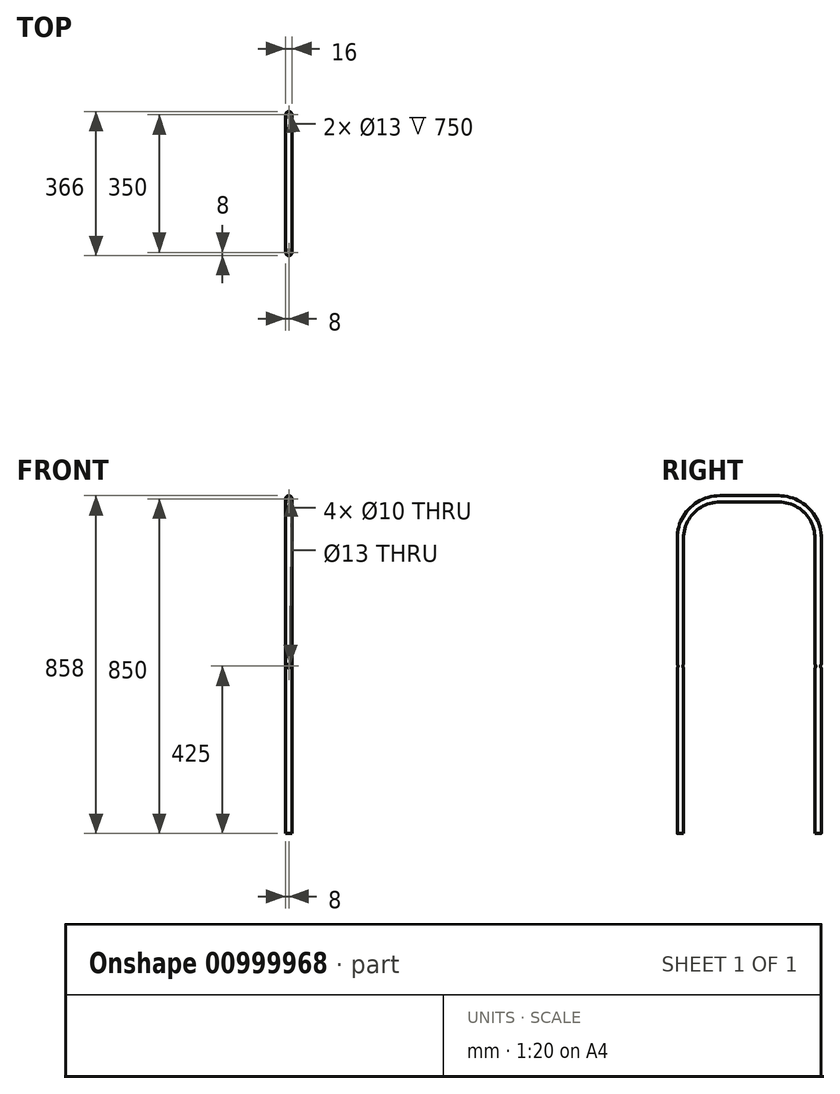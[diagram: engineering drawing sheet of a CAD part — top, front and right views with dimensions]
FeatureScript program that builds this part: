
annotation { "Feature Type Name" : "Feature", "Feature Type Description" : "" }
export const myFeature = defineFeature(function(context is Context, id is Id, definition is map)
    precondition{}
    {
        {
            var Q0;
            Q0=qCreatedBy(makeId("Right.planeOp"),FACE);
            var sketch = newSketch(context, id + "F0", { "sketchPlane" : qUnion([Q0])});
            skLineSegment(sketch, "E0.top", {"start": v(-100, 850) * mm, "end": v(-250, 850) * mm});
            skLineSegment(sketch, "E0.left", {"start": v(0, 0) * mm, "end": v(0, 750) * mm});
            skLineSegment(sketch, "E0.right", {"start": v(-350, 0) * mm, "end": v(-350, 750) * mm});
            skPoint(sketch, "E1.visualSharp", {"position": v(-350, 850) * mm});
            skArc(sketch, "E1.filletArc", {"start": v(-250, 850) * mm, "mid": v(-320.71, 820.71) * mm, "end": v(-350, 750) * mm});
            skPoint(sketch, "E2.visualSharp", {"position": v(0, 850) * mm});
            skArc(sketch, "E2.filletArc", {"start": v(0, 750) * mm, "mid": v(-29.29, 820.71) * mm, "end": v(-100, 850) * mm});
            skPoint(sketch, "E3.visualSharp", {"position": v(-16, 884) * mm});
            skPoint(sketch, "E4.visualSharp", {"position": v(-334, 884) * mm});
            skSolve(sketch);
        }
        {
            var Q0;
            Q0=qCreatedBy(makeId("Top.planeOp"),FACE);
            var sketch = newSketch(context, id + "F1", { "sketchPlane" : qUnion([Q0])});
            skCircle(sketch, "E5", {"center": v(0, 0) * mm, "radius": 8 * mm});
            skSolve(sketch);
        }
        {
            var Q0;
            Q0=makeQuery(id+"F1.imprint","IMPRINT",FACE,{"disambiguationData":[TD([[makeQuery(id+"F1.imprint","IMPRINT",EDGE,{"derivedFrom":sQuery(id+"F1.wireOp",EDGE,"E5")}),1.0]])]});
            var Q1;
            Q1=sQuery(id+"F0.wireOp",EDGE,"E0.left");
            var Q2;
            Q2=sQuery(id+"F0.wireOp",EDGE,"E2.filletArc");
            var Q3;
            Q3=sQuery(id+"F0.wireOp",EDGE,"E0.top");
            var Q4;
            Q4=sQuery(id+"F0.wireOp",EDGE,"E1.filletArc");
            var Q5;
            Q5=sQuery(id+"F0.wireOp",EDGE,"E0.right");
            sweep(context, id + "F2", {"profiles" : qUnion([Q0]), "path" : qUnion([Q1, Q2, Q3, Q4, Q5])});
        }
        {
            var Q0;
            Q0=makeQuery(id+"F2.opSweep","CAP_FACE",FACE,{"disambiguationData":[OSD([sQuery(id+"F0.wireOp",VERTEX,"E0.right.start"),sQuery(id+"F1.wireOp",EDGE,"E5")])],"isStart":false});
            var Q1;
            Q1=makeQuery(id+"F2.opSweep","CAP_FACE",FACE,{"disambiguationData":[OSD([sQuery(id+"F0.wireOp",VERTEX,"E0.left.start"),sQuery(id+"F1.wireOp",EDGE,"E5")])],"isStart":true});
            shell(context, id + "F3", {"entities" : qUnion([Q0, Q1]), "thickness" : 1.5 * mm});
        }
        {
            var Q0;
            Q0=qCreatedBy(makeId("Front.planeOp"),FACE);
            var sketch = newSketch(context, id + "F4", { "sketchPlane" : qUnion([Q0])});
            skLineSegment(sketch, "E6", {"start": v(0, 700) * mm, "end": v(0, 0) * mm});
            skLineSegment(sketch, "E7", {"start": v(0, 350) * mm, "end": v(0, 700) * mm});
            skLineSegment(sketch, "E8", {"start": v(0, 425) * mm, "end": v(108.7, 425) * mm});
            skSolve(sketch);
        }
        {
            var Q0;
            Q0=sQuery(id+"F4.wireOp",VERTEX,"E8.start");
            var Q1;
            Q1=makeQuery(id+"F2.opSweep","SWEPT_BODY",BODY,{"disambiguationData":[OSD([sQuery(id+"F0.wireOp",EDGE,"E0.right"),sQuery(id+"F1.wireOp",EDGE,"E5")])]});
            hole(context, id + "F5", {"style" : HoleStyle.SIMPLE, "endStyle" : HoleEndStyle.THROUGH, "oppositeDirection" : true, "holeDiameter" : 10 * mm, "majorDiameter" : 5 * mm, "isTappedThrough" : true, "tappedDepth" : 12 * mm, "tapClearance" : 3, "locations" : qUnion([Q0]), "scope" : qUnion([Q1])});
        }
        {
            var Q0;
            Q0=sQuery(id+"F4.wireOp",VERTEX,"E8.start");
            var Q1;
            Q1=makeQuery(id+"F2.opSweep","SWEPT_BODY",BODY,{"disambiguationData":[OSD([sQuery(id+"F0.wireOp",EDGE,"E0.right"),sQuery(id+"F1.wireOp",EDGE,"E5")])]});
            hole(context, id + "F6", {"style" : HoleStyle.SIMPLE, "endStyle" : HoleEndStyle.THROUGH, "holeDiameter" : 10 * mm, "majorDiameter" : 5 * mm, "isTappedThrough" : true, "tappedDepth" : 12 * mm, "tapClearance" : 3, "locations" : qUnion([Q0]), "scope" : qUnion([Q1])});
        }
    });
